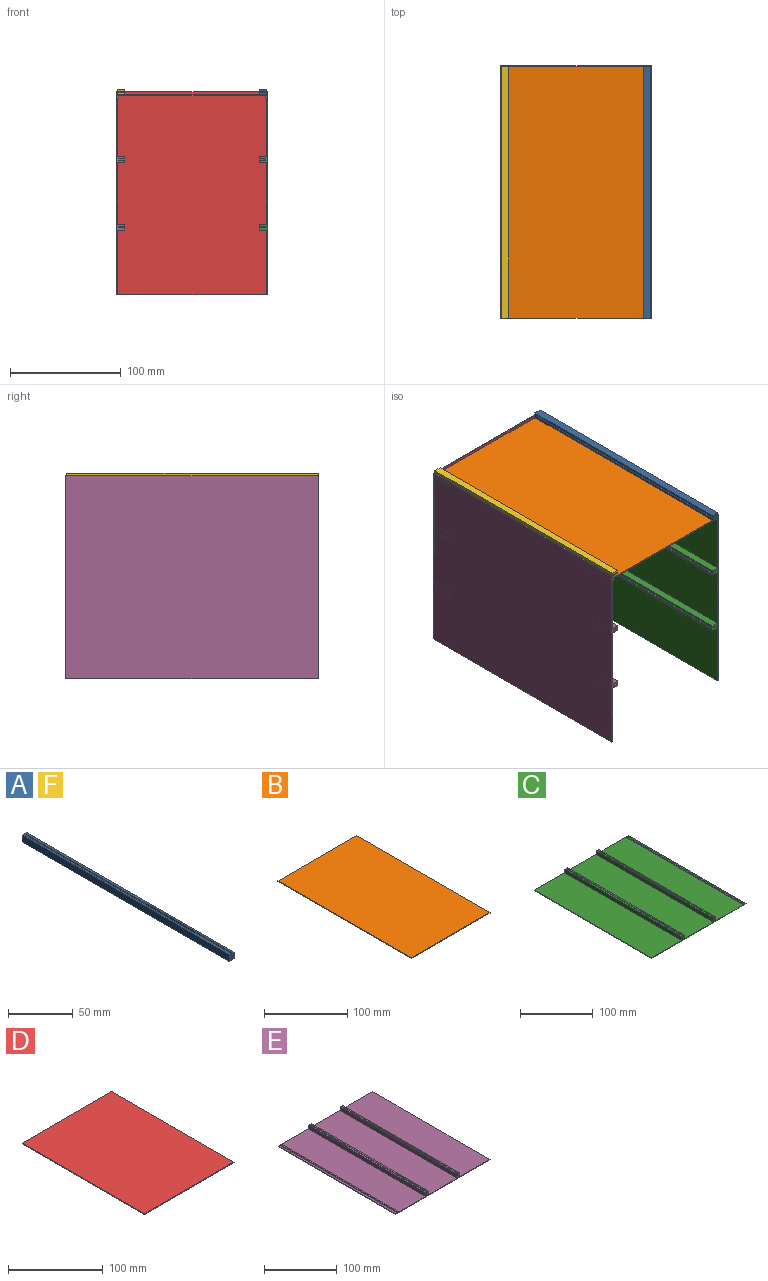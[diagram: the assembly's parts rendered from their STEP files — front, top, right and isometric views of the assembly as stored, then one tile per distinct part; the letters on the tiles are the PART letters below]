
ASSEMBLY  parts=6 mates=13
PART A: 14 faces, bbox 5.2x226.7x6.5 mm
  f0: plane 220.71x1.2mm, normal (0,0,1), area 264.9mm2, adj f7,f8,f9,f11
  f1: plane 226.71x5.2mm, normal (0,0,-1), area 1176.4mm2, adj f3,f4,f5,f6,f7,f8,f11,f12
  f2: plane 1.2x0.9mm, normal (0,0,1), area 1.1mm2, adj f7,f8,f12,f13
  f3: plane 6.5x5.2mm, normal (0,1,0), area 33.8mm2, adj f1,f4,f6,f10
  f4: plane 226.71x6.5mm, normal (-1,0,0), area 1473.6mm2, adj f1,f3,f5,f10
  f5: plane 6.5x5.2mm, normal (0,-1,0), area 27.2mm2, adj f1,f4,f6,f7,f8,f10,f13
  f6: plane 226.71x6.5mm, normal (1,0,0), area 1473.6mm2, adj f1,f3,f5,f10
  f7: plane 224.71x6.5mm, normal (-1,0,0), area 1015.9mm2, adj f0,f1,f2,f5,f9,f10,f11,f12
  f8: plane 224.71x6.5mm, normal (1,0,0), area 1015.9mm2, adj f0,f1,f2,f5,f9,f10,f11,f12
  f9: plane 4.5x1.2mm, normal (0,-1,0), area 5.4mm2, adj f0,f7,f8,f10
  f10: plane 226.71x5.2mm, normal (0,0,1), area 909.2mm2, adj f3,f4,f5,f6,f7,f8,f9
  f11: plane 2x1.2mm, normal (0,-1,0), area 2.4mm2, adj f0,f1,f7,f8
  f12: plane 2x1.2mm, normal (0,1,0), area 2.4mm2, adj f1,f2,f7,f8
  f13: plane 1.2x1mm, normal (0,-0.71,0.71), area 1.7mm2, adj f2,f5,f7,f8
PART B: 6 faces, bbox 134x226.7x1 mm
  f0: plane 134x1mm, normal (0,1,0), area 134mm2, adj f1,f3,f4,f5
  f1: plane 226.71x1mm, normal (-1,0,0), area 226.7mm2, adj f0,f2,f4,f5
  f2: plane 134x1mm, normal (0,-1,0), area 134mm2, adj f1,f3,f4,f5
  f3: plane 226.71x1mm, normal (1,0,0), area 226.7mm2, adj f0,f2,f4,f5
  f4: plane 226.71x134mm, normal (0,0,1), area 30379.1mm2, adj f0,f1,f2,f3
  f5: plane 226.71x134mm, normal (0,0,-1), area 30379.1mm2, adj f0,f1,f2,f3
PART C: 36 faces, bbox 183x227.7x7.5 mm
  f0: plane 227.71x183mm, normal (0,0,1), area 38859.7mm2, adj f3,f4,f5,f6,f14,f15,f16,f18
  f1: plane 220.71x1.2mm, normal (0,0,1), area 264.9mm2, adj f7,f8,f9,f11
  f2: plane 1.2x0.9mm, normal (0,0,1), area 1.1mm2, adj f7,f8,f12,f35
  f3: plane 226.71x6.5mm, normal (-1,0,0), area 1473.6mm2, adj f0,f4,f6,f10
  f4: plane 183x7.5mm, normal (0,-1,0), area 239.4mm2, adj f0,f3,f5,f7,f8,f10,f15,f16
  f5: plane 226.71x6.5mm, normal (1,0,0), area 1473.6mm2, adj f0,f4,f6,f10
  f6: plane 6.5x5.2mm, normal (0,1,0), area 33.8mm2, adj f0,f3,f5,f10
  f7: plane 224.71x6.5mm, normal (-1,0,0), area 1015.9mm2, adj f1,f2,f4,f9,f10,f11,f12,f13
  f8: plane 224.71x6.5mm, normal (1,0,0), area 1015.9mm2, adj f1,f2,f4,f9,f10,f11,f12,f13
  f9: plane 4.5x1.2mm, normal (0,-1,0), area 5.4mm2, adj f1,f7,f8,f10
  f10: plane 226.71x5.2mm, normal (0,0,1), area 909.2mm2, adj f3,f4,f5,f6,f7,f8,f9
  f11: plane 2x1.2mm, normal (0,-1,0), area 2.4mm2, adj f1,f7,f8,f13
  f12: plane 2x1.2mm, normal (0,1,0), area 2.4mm2, adj f2,f7,f8,f13
  f13: plane 2.1x1.2mm, normal (0,0,1), area 2.5mm2, adj f7,f8,f11,f12
  f14: plane 183x1mm, normal (0,1,0), area 183mm2, adj f0,f15,f16,f17
  f15: plane 227.71x1mm, normal (-1,0,0), area 227.7mm2, adj f0,f4,f14,f17
  f16: plane 227.71x1mm, normal (1,0,0), area 227.7mm2, adj f0,f4,f14,f17
  f17: plane 227.71x183mm, normal (0,0,-1), area 41670.9mm2, adj f4,f14,f15,f16
  f18: plane 226.71x1mm, normal (1,0,0), area 226.7mm2, adj f0,f4,f19,f21
  f19: plane 2x1mm, normal (0,1,0), area 2mm2, adj f0,f18,f20,f21
  f20: plane 226.71x1mm, normal (-1,0,0), area 226.7mm2, adj f0,f4,f19,f21
  f21: plane 226.71x2mm, normal (0,0,1), area 453.4mm2, adj f4,f18,f19,f20
  f22: plane 224.71x6.5mm, normal (-1,0,0), area 1015.9mm2, adj f4,f27,f28,f29,f30,f31,f32,f33
  f23: plane 226.71x6.5mm, normal (1,0,0), area 1473.6mm2, adj f0,f4,f24,f28
  f24: plane 6.5x5.2mm, normal (0,1,0), area 33.8mm2, adj f0,f23,f25,f28
  f25: plane 226.71x6.5mm, normal (-1,0,0), area 1473.6mm2, adj f0,f4,f24,f28
  f26: plane 224.71x6.5mm, normal (1,0,0), area 1015.9mm2, adj f4,f27,f28,f29,f30,f31,f32,f33
  f27: plane 4.5x1.2mm, normal (0,-1,0), area 5.4mm2, adj f22,f26,f28,f30
  f28: plane 226.71x5.2mm, normal (0,0,1), area 909.2mm2, adj f4,f22,f23,f24,f25,f26,f27
  f29: plane 1.2x0.9mm, normal (0,0,1), area 1.1mm2, adj f22,f26,f31,f34
  f30: plane 220.71x1.2mm, normal (0,0,1), area 264.9mm2, adj f22,f26,f27,f32
  f31: plane 2x1.2mm, normal (0,1,0), area 2.4mm2, adj f22,f26,f29,f33
  f32: plane 2x1.2mm, normal (0,-1,0), area 2.4mm2, adj f22,f26,f30,f33
  f33: plane 2.1x1.2mm, normal (0,0,1), area 2.5mm2, adj f22,f26,f31,f32
  f34: plane 1.2x1mm, normal (0,-0.71,0.71), area 1.7mm2, adj f4,f22,f26,f29
  f35: plane 1.2x1mm, normal (0,-0.71,0.71), area 1.7mm2, adj f2,f4,f7,f8
PART D: 6 faces, bbox 134x183x1 mm
  f0: plane 134x1mm, normal (0,1,0), area 134mm2, adj f1,f3,f4,f5
  f1: plane 183x1mm, normal (-1,0,0), area 183mm2, adj f0,f2,f4,f5
  f2: plane 134x1mm, normal (0,-1,0), area 134mm2, adj f1,f3,f4,f5
  f3: plane 183x1mm, normal (1,0,0), area 183mm2, adj f0,f2,f4,f5
  f4: plane 183x134mm, normal (0,0,1), area 24522mm2, adj f0,f1,f2,f3
  f5: plane 183x134mm, normal (0,0,-1), area 24522mm2, adj f0,f1,f2,f3
PART E: 36 faces, bbox 183x227.7x7.5 mm
  f0: plane 224.71x6.5mm, normal (-1,0,0), area 1015.9mm2, adj f4,f6,f7,f8,f9,f10,f11,f12
  f1: plane 226.71x6.5mm, normal (1,0,0), area 1473.6mm2, adj f2,f4,f7,f13
  f2: plane 6.5x5.2mm, normal (0,1,0), area 33.8mm2, adj f1,f3,f7,f13
  f3: plane 226.71x6.5mm, normal (-1,0,0), area 1473.6mm2, adj f2,f4,f7,f13
  f4: plane 183x7.5mm, normal (0,-1,0), area 239.4mm2, adj f0,f1,f3,f5,f7,f13,f17,f18
  f5: plane 224.71x6.5mm, normal (1,0,0), area 1015.9mm2, adj f4,f6,f7,f8,f9,f10,f11,f12
  f6: plane 4.5x1.2mm, normal (0,-1,0), area 5.4mm2, adj f0,f5,f7,f9
  f7: plane 226.71x5.2mm, normal (0,0,1), area 909.2mm2, adj f0,f1,f2,f3,f4,f5,f6
  f8: plane 1.2x0.9mm, normal (0,0,1), area 1.1mm2, adj f0,f5,f10,f34
  f9: plane 220.71x1.2mm, normal (0,0,1), area 264.9mm2, adj f0,f5,f6,f11
  f10: plane 2x1.2mm, normal (0,1,0), area 2.4mm2, adj f0,f5,f8,f12
  f11: plane 2x1.2mm, normal (0,-1,0), area 2.4mm2, adj f0,f5,f9,f12
  f12: plane 2.1x1.2mm, normal (0,0,1), area 2.5mm2, adj f0,f5,f10,f11
  f13: plane 227.71x183mm, normal (0,0,1), area 38859.7mm2, adj f1,f2,f3,f4,f16,f17,f18,f26
  f14: plane 220.71x1.2mm, normal (0,0,1), area 264.9mm2, adj f19,f20,f21,f23
  f15: plane 1.2x0.9mm, normal (0,0,1), area 1.1mm2, adj f19,f20,f24,f35
  f16: plane 6.5x5.2mm, normal (0,1,0), area 33.8mm2, adj f13,f17,f18,f22
  f17: plane 226.71x6.5mm, normal (-1,0,0), area 1473.6mm2, adj f4,f13,f16,f22
  f18: plane 226.71x6.5mm, normal (1,0,0), area 1473.6mm2, adj f4,f13,f16,f22
  f19: plane 224.71x6.5mm, normal (-1,0,0), area 1015.9mm2, adj f4,f14,f15,f21,f22,f23,f24,f25
  f20: plane 224.71x6.5mm, normal (1,0,0), area 1015.9mm2, adj f4,f14,f15,f21,f22,f23,f24,f25
  f21: plane 4.5x1.2mm, normal (0,-1,0), area 5.4mm2, adj f14,f19,f20,f22
  f22: plane 226.71x5.2mm, normal (0,0,1), area 909.2mm2, adj f4,f16,f17,f18,f19,f20,f21
  f23: plane 2x1.2mm, normal (0,-1,0), area 2.4mm2, adj f14,f19,f20,f25
  f24: plane 2x1.2mm, normal (0,1,0), area 2.4mm2, adj f15,f19,f20,f25
  f25: plane 2.1x1.2mm, normal (0,0,1), area 2.5mm2, adj f19,f20,f23,f24
  f26: plane 227.71x1mm, normal (-1,0,0), area 227.7mm2, adj f4,f13,f28,f29
  f27: plane 227.71x1mm, normal (1,0,0), area 227.7mm2, adj f4,f13,f28,f29
  f28: plane 183x1mm, normal (0,1,0), area 183mm2, adj f13,f26,f27,f29
  f29: plane 227.71x183mm, normal (0,0,-1), area 41670.9mm2, adj f4,f26,f27,f28
  f30: plane 226.71x1mm, normal (-1,0,0), area 226.7mm2, adj f4,f13,f32,f33
  f31: plane 226.71x1mm, normal (1,0,0), area 226.7mm2, adj f4,f13,f32,f33
  f32: plane 2x1mm, normal (0,1,0), area 2mm2, adj f13,f30,f31,f33
  f33: plane 226.71x2mm, normal (0,0,1), area 453.4mm2, adj f4,f30,f31,f32
  f34: plane 1.2x1mm, normal (0,-0.71,0.71), area 1.7mm2, adj f0,f4,f5,f8
  f35: plane 1.2x1mm, normal (0,-0.71,0.71), area 1.7mm2, adj f4,f15,f19,f20
PART F: same geometry as A
PLACE A rot(axis=(0,-1,0),90deg) t=(140.76,-97.72,185.75)mm
PLACE B t=(3.04,-97.72,184.75)mm
PLACE C rot(axis=(0,-1,0),90deg) t=(140.76,-97.72,2.75)mm
PLACE D rot(axis=(-1,0,0),90deg) t=(6.76,128.99,188.25)mm
PLACE E rot(axis=(0,1,0),90deg) t=(6.76,-97.72,129.95)mm
PLACE F rot(axis=(0,1,0),90deg) t=(6.76,-97.72,190.95)mm
MATE planar E.f4 <-> C.f4  axis (0,-1,0) through (6.76,-97.72,129.95)mm
MATE planar E.f27 <-> D.f0  axis (0,0,-1) through (6.26,16.14,5.25)mm
MATE planar F.f6 <-> B.f4  axis (0,0,-1) through (10.01,15.64,185.75)mm
MATE planar B.f5 <-> C.f18  axis (0,0,-1) through (73.76,15.64,184.75)mm
MATE planar E.f13 <-> F.f1  axis (1,0,0) through (6.76,16.17,95.73)mm
MATE planar D.f5 <-> C.f6  axis (0,-1,0) through (73.76,128.99,96.75)mm
MATE planar E.f13 <-> B.f1  axis (1,0,0) through (6.76,15.64,63.75)mm
MATE planar B.f5 <-> E.f30  axis (0,0,-1) through (73.76,128.99,184.75)mm
MATE planar B.f3 <-> C.f0  axis (1,0,0) through (140.76,15.64,185.25)mm
MATE planar A.f1 <-> C.f0  axis (1,0,0) through (140.76,15.88,188.35)mm
MATE planar B.f4 <-> A.f4  axis (0,0,1) through (73.76,15.64,185.75)mm
MATE planar D.f1 <-> E.f13  axis (-1,0,0) through (6.76,129.49,96.75)mm
MATE planar C.f4 <-> B.f2  axis (0,-1,0) through (140.76,-97.72,184.75)mm
